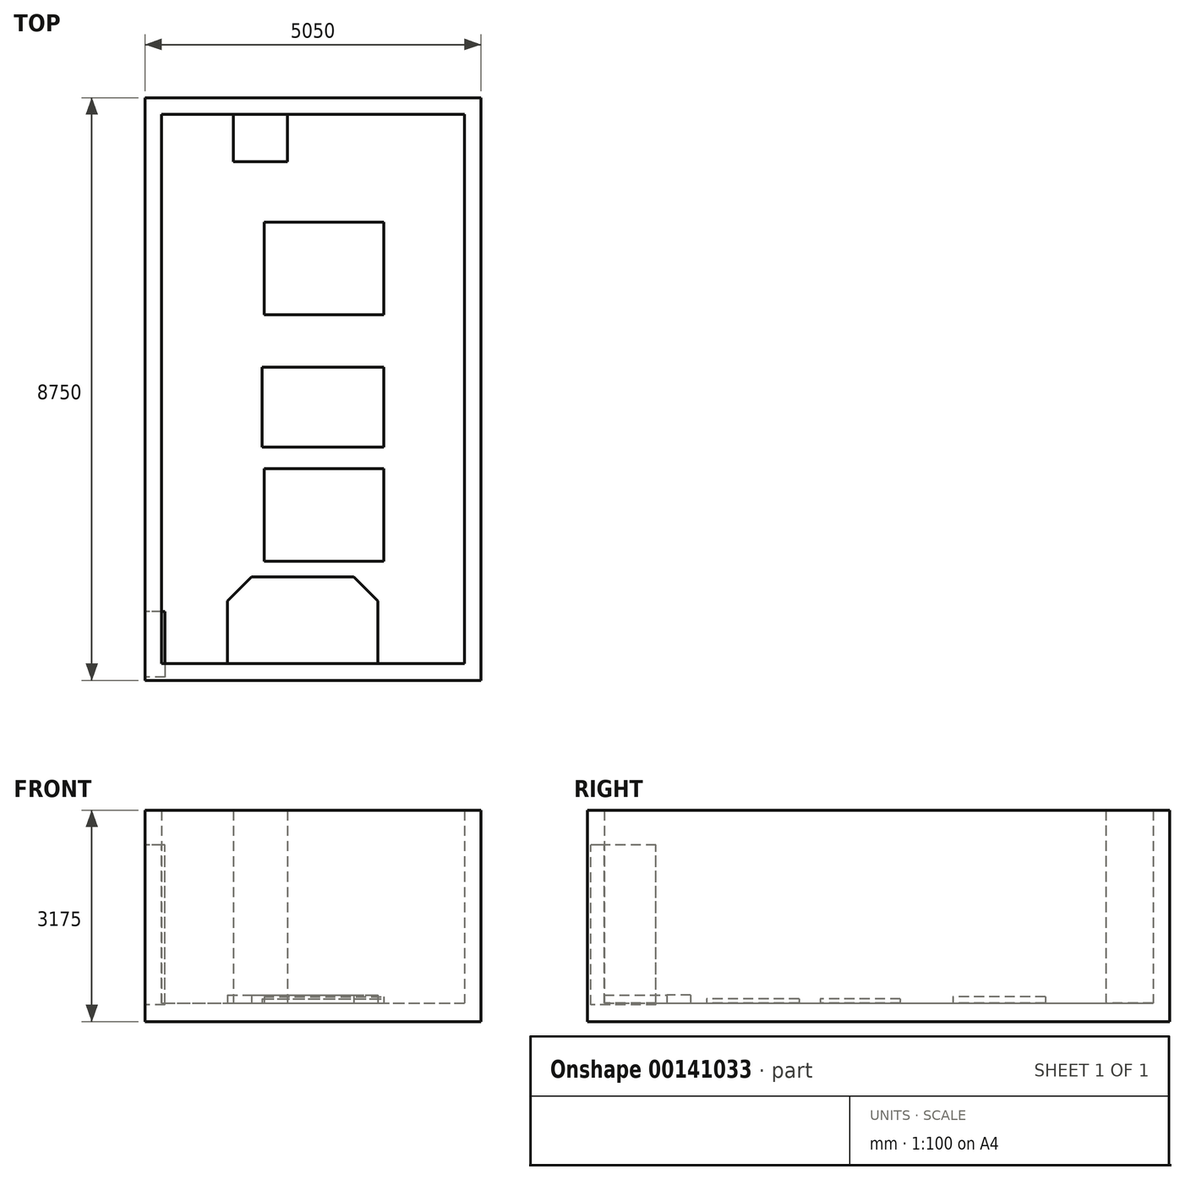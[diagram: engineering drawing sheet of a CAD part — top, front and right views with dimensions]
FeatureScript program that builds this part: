
annotation { "Feature Type Name" : "Feature", "Feature Type Description" : "" }
export const myFeature = defineFeature(function(context is Context, id is Id, definition is map)
    precondition{}
    {
        {
            var Q0;
            Q0=qCreatedBy(makeId("Top.planeOp"),FACE);
            var sketch = newSketch(context, id + "F0", { "sketchPlane" : qUnion([Q0])});
            skLineSegment(sketch, "E0.bottom", {"start": v(0, 0) * mm, "end": v(4550, 0) * mm});
            skLineSegment(sketch, "E0.top", {"start": v(0, 8250) * mm, "end": v(4550, 8250) * mm});
            skLineSegment(sketch, "E0.left", {"start": v(0, 0) * mm, "end": v(0, 8250) * mm});
            skLineSegment(sketch, "E0.right", {"start": v(4550, 0) * mm, "end": v(4550, 8250) * mm});
            skSolve(sketch);
        }
        {
            var Q0;
            Q0=qSketchRegion(id+"F0",true);
            extrude(context, id + "F1", {"entities" : qUnion([Q0]), "depth" : 2920 * mm});
        }
        {
            var Q0;
            Q0=makeQuery(id+"F1.opExtrude","CAP_FACE",FACE,{"disambiguationData":[OSD([sQuery(id+"F0.wireOp",EDGE,"E0.bottom"),sQuery(id+"F0.wireOp",EDGE,"E0.top"),sQuery(id+"F0.wireOp",EDGE,"E0.left"),sQuery(id+"F0.wireOp",EDGE,"E0.right")])],"isStart":false});
            shell(context, id + "F2", {"entities" : qUnion([Q0]), "thickness" : 250 * mm, "oppositeDirection" : true});
        }
        {
            var Q0;
            Q0=makeQuery(id+"F2.opShell","OFFSET_FACE",FACE,{"disambiguationData":[OSD([sQuery(id+"F0.wireOp",EDGE,"E0.bottom"),sQuery(id+"F0.wireOp",EDGE,"E0.top"),sQuery(id+"F0.wireOp",EDGE,"E0.left"),sQuery(id+"F0.wireOp",EDGE,"E0.right")])]});
            var sketch = newSketch(context, id + "F3", { "sketchPlane" : qUnion([Q0])});
            skLineSegment(sketch, "E1.bottom", {"start": v(1540, 2930) * mm, "end": v(3340, 2930) * mm});
            skLineSegment(sketch, "E1.top", {"start": v(1540, 1540) * mm, "end": v(3340, 1540) * mm});
            skLineSegment(sketch, "E1.left", {"start": v(1540, 2930) * mm, "end": v(1540, 1540) * mm});
            skLineSegment(sketch, "E1.right", {"start": v(3340, 2930) * mm, "end": v(3340, 1540) * mm});
            skSolve(sketch);
        }
        {
            var Q0;
            Q0=qSketchRegion(id+"F3",true);
            extrude(context, id + "F4", {"entities" : qUnion([Q0]), "operationType" : NewBodyOperationType.ADD, "depth" : 90 * mm});
        }
        {
            var Q0;
            Q0=makeQuery(id+"F2.opShell","OFFSET_FACE",FACE,{"disambiguationData":[OSD([sQuery(id+"F0.wireOp",EDGE,"E0.bottom"),sQuery(id+"F0.wireOp",EDGE,"E0.top"),sQuery(id+"F0.wireOp",EDGE,"E0.left"),sQuery(id+"F0.wireOp",EDGE,"E0.right")])]});
            var sketch = newSketch(context, id + "F5", { "sketchPlane" : qUnion([Q0])});
            skLineSegment(sketch, "E2.bottom", {"start": v(1510, 4450) * mm, "end": v(3340, 4450) * mm});
            skLineSegment(sketch, "E2.top", {"start": v(1510, 3250) * mm, "end": v(3340, 3250) * mm});
            skLineSegment(sketch, "E2.left", {"start": v(1510, 4450) * mm, "end": v(1510, 3250) * mm});
            skLineSegment(sketch, "E2.right", {"start": v(3340, 4450) * mm, "end": v(3340, 3250) * mm});
            skSolve(sketch);
        }
        {
            var Q0;
            Q0=qSketchRegion(id+"F5",true);
            extrude(context, id + "F6", {"entities" : qUnion([Q0]), "operationType" : NewBodyOperationType.ADD, "depth" : 90 * mm});
        }
        {
            var Q0;
            Q0=makeQuery(id+"F2.opShell","OFFSET_FACE",FACE,{"disambiguationData":[OSD([sQuery(id+"F0.wireOp",EDGE,"E0.bottom"),sQuery(id+"F0.wireOp",EDGE,"E0.top"),sQuery(id+"F0.wireOp",EDGE,"E0.left"),sQuery(id+"F0.wireOp",EDGE,"E0.right")])]});
            var sketch = newSketch(context, id + "F7", { "sketchPlane" : qUnion([Q0])});
            skLineSegment(sketch, "E3.bottom", {"start": v(1540, 6630) * mm, "end": v(3340, 6630) * mm});
            skLineSegment(sketch, "E3.top", {"start": v(1540, 5240) * mm, "end": v(3340, 5240) * mm});
            skLineSegment(sketch, "E3.left", {"start": v(1540, 6630) * mm, "end": v(1540, 5240) * mm});
            skLineSegment(sketch, "E3.right", {"start": v(3340, 6630) * mm, "end": v(3340, 5240) * mm});
            skSolve(sketch);
        }
        {
            var Q0;
            Q0=qSketchRegion(id+"F7",true);
            extrude(context, id + "F8", {"entities" : qUnion([Q0]), "operationType" : NewBodyOperationType.ADD, "depth" : 120 * mm});
        }
        {
            var Q0;
            Q0=makeQuery(id+"F2.opShell","OFFSET_FACE",FACE,{"disambiguationData":[OSD([sQuery(id+"F0.wireOp",EDGE,"E0.bottom"),sQuery(id+"F0.wireOp",EDGE,"E0.top"),sQuery(id+"F0.wireOp",EDGE,"E0.left"),sQuery(id+"F0.wireOp",EDGE,"E0.right")])]});
            var sketch = newSketch(context, id + "F9", { "sketchPlane" : qUnion([Q0])});
            skLineSegment(sketch, "E4", {"start": v(990, 0) * mm, "end": v(990, 940) * mm});
            skLineSegment(sketch, "E5", {"start": v(990, 940) * mm, "end": v(1351.25, 1300) * mm});
            skLineSegment(sketch, "E6", {"start": v(1351.25, 1300) * mm, "end": v(2888.75, 1300) * mm});
            skLineSegment(sketch, "E7", {"start": v(2888.75, 1300) * mm, "end": v(3250, 940) * mm});
            skLineSegment(sketch, "E8", {"start": v(3250, 940) * mm, "end": v(3250, 0) * mm});
            skLineSegment(sketch, "E9", {"start": v(3250, 0) * mm, "end": v(990, 0) * mm});
            skSolve(sketch);
        }
        {
            var Q0;
            Q0=qSketchRegion(id+"F9",true);
            extrude(context, id + "F10", {"entities" : qUnion([Q0]), "operationType" : NewBodyOperationType.ADD, "depth" : 150 * mm});
        }
        {
            var Q0;
            Q0=makeQuery(id+"F2.opShell","OFFSET_FACE",FACE,{"disambiguationData":[OSD([sQuery(id+"F0.wireOp",EDGE,"E0.bottom"),sQuery(id+"F0.wireOp",EDGE,"E0.top"),sQuery(id+"F0.wireOp",EDGE,"E0.left"),sQuery(id+"F0.wireOp",EDGE,"E0.right")])]});
            extrude(context, id + "F11", {"entities" : qUnion([Q0]), "operationType" : NewBodyOperationType.ADD, "depth" : 25 * mm});
        }
        {
            var Q0;
            Q0=makeQuery(id+"F11.opExtrude","CAP_FACE",FACE,{"disambiguationData":[OSD([sQuery(id+"F0.wireOp",EDGE,"E0.bottom"),sQuery(id+"F0.wireOp",EDGE,"E0.top"),sQuery(id+"F0.wireOp",EDGE,"E0.left"),sQuery(id+"F0.wireOp",EDGE,"E0.right")])],"isStart":false});
            var sketch = newSketch(context, id + "F12", { "sketchPlane" : qUnion([Q0])});
            skLineSegment(sketch, "E10.bottom", {"start": v(1077, 8250) * mm, "end": v(1887, 8250) * mm});
            skLineSegment(sketch, "E10.top", {"start": v(1077, 7540) * mm, "end": v(1887, 7540) * mm});
            skLineSegment(sketch, "E10.left", {"start": v(1077, 8250) * mm, "end": v(1077, 7540) * mm});
            skLineSegment(sketch, "E10.right", {"start": v(1887, 8250) * mm, "end": v(1887, 7540) * mm});
            skSolve(sketch);
        }
        {
            var Q0;
            Q0=qSketchRegion(id+"F12",true);
            extrude(context, id + "F13", {"entities" : qUnion([Q0]), "operationType" : NewBodyOperationType.ADD, "depth" : 2900 * mm});
        }
        {
            var Q0;
            Q0=makeQuery(id+"F1.opExtrude","SWEPT_FACE",FACE,{"disambiguationData":[OSD([sQuery(id+"F0.wireOp",EDGE,"E0.left")])]});
            var sketch = newSketch(context, id + "F14", { "sketchPlane" : qUnion([Q0])});
            skLineSegment(sketch, "E11.bottom", {"start": v(-780, 0) * mm, "end": v(200, 0) * mm});
            skLineSegment(sketch, "E11.top", {"start": v(-780, 2400) * mm, "end": v(200, 2400) * mm});
            skLineSegment(sketch, "E11.left", {"start": v(-780, 0) * mm, "end": v(-780, 2400) * mm});
            skLineSegment(sketch, "E11.right", {"start": v(200, 0) * mm, "end": v(200, 2400) * mm});
            skSolve(sketch);
        }
        {
            var Q0;
            Q0=qSketchRegion(id+"F14",true);
            extrude(context, id + "F15", {"entities" : qUnion([Q0]), "operationType" : NewBodyOperationType.REMOVE, "oppositeDirection" : true, "depth" : 300 * mm});
        }
    });
